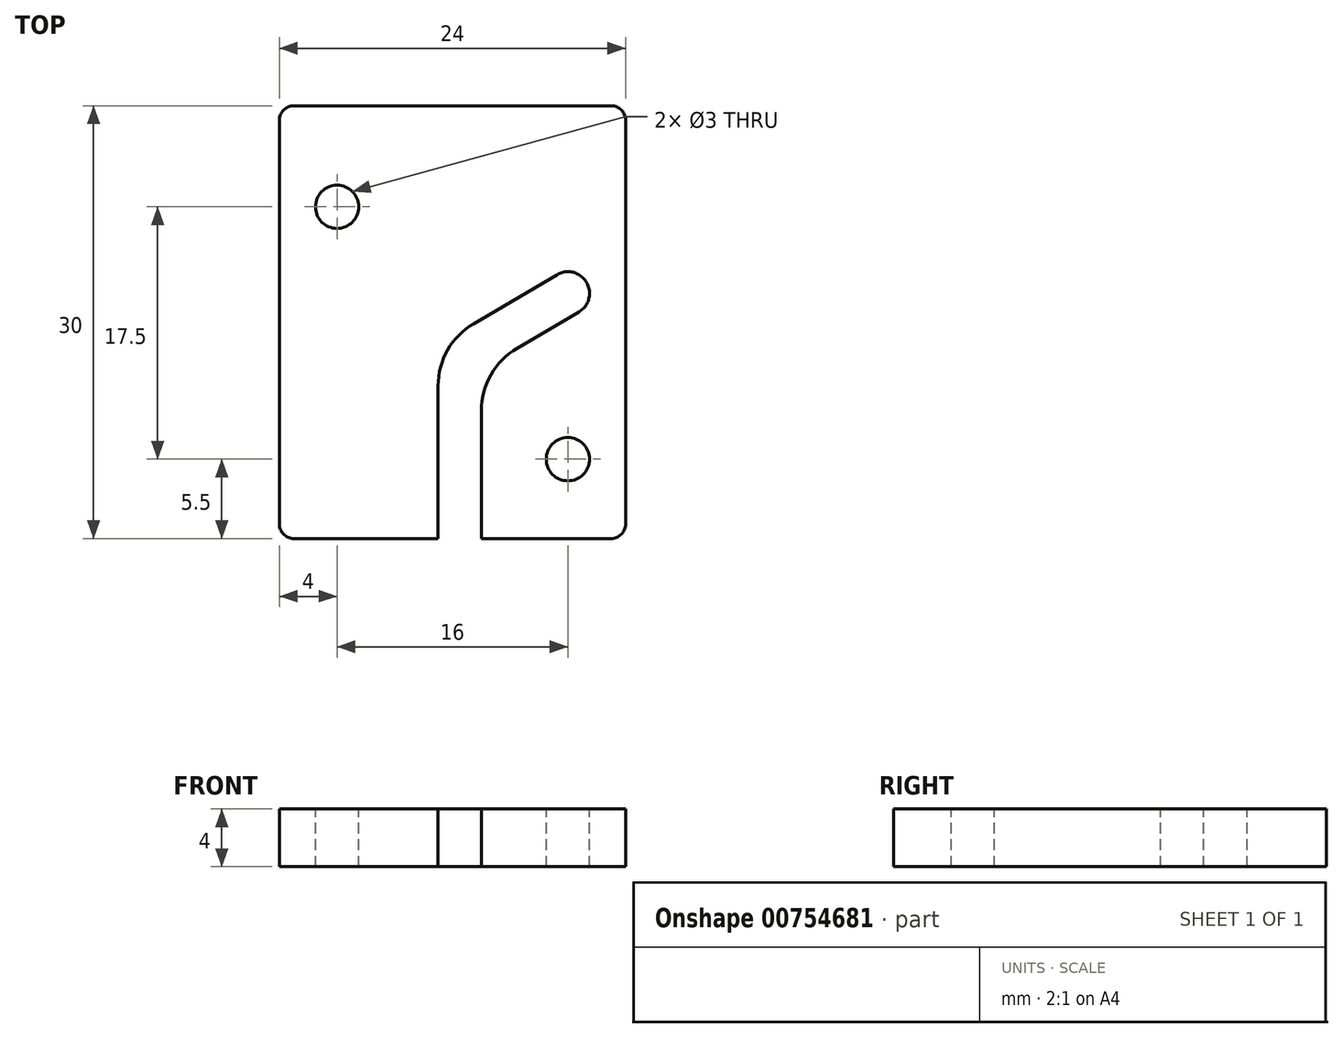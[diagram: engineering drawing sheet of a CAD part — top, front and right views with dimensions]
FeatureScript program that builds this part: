
annotation { "Feature Type Name" : "Feature", "Feature Type Description" : "" }
export const myFeature = defineFeature(function(context is Context, id is Id, definition is map)
    precondition{}
    {
        {
            var Q0;
            Q0=qCreatedBy(makeId("Top.planeOp"),FACE);
            var sketch = newSketch(context, id + "F0", { "sketchPlane" : qUnion([Q0])});
            skLineSegment(sketch, "E0.bottom", {"start": v(1, 0) * mm, "end": v(23, 0) * mm});
            skLineSegment(sketch, "E0.top", {"start": v(1, 30) * mm, "end": v(23, 30) * mm});
            skLineSegment(sketch, "E0.left", {"start": v(0, 1) * mm, "end": v(0, 29) * mm});
            skLineSegment(sketch, "E0.right", {"start": v(24, 1) * mm, "end": v(24, 29) * mm});
            skLineSegment(sketch, "E1", {"start": v(14, 0) * mm, "end": v(14, 8.87) * mm});
            skLineSegment(sketch, "E2", {"start": v(11, 0) * mm, "end": v(11, 10.59) * mm});
            skPoint(sketch, "E3", {"position": v(20, 17) * mm});
            skArc(sketch, "E4", {"start": v(20.76, 15.7) * mm, "mid": v(21.3, 17.76) * mm, "end": v(19.24, 18.3) * mm});
            skLineSegment(sketch, "E5", {"start": v(19.24, 18.3) * mm, "end": v(13.46, 14.9) * mm});
            skLineSegment(sketch, "E6", {"start": v(20.76, 15.7) * mm, "end": v(16.46, 13.18) * mm});
            skArc(sketch, "E7.filletArc", {"start": v(16.46, 13.18) * mm, "mid": v(14.66, 11.35) * mm, "end": v(14, 8.87) * mm});
            skArc(sketch, "E8.filletArc", {"start": v(13.46, 14.9) * mm, "mid": v(11.66, 13.07) * mm, "end": v(11, 10.59) * mm});
            skPoint(sketch, "E9.visualSharp", {"position": v(0, 30) * mm});
            skArc(sketch, "E9.filletArc", {"start": v(1, 30) * mm, "mid": v(0.3, 29.7) * mm, "end": v(0, 29) * mm});
            skPoint(sketch, "E10.visualSharp", {"position": v(0, 0) * mm});
            skArc(sketch, "E10.filletArc", {"start": v(0, 1) * mm, "mid": v(0.3, 0.3) * mm, "end": v(1, 0) * mm});
            skPoint(sketch, "E11.visualSharp", {"position": v(24, 0) * mm});
            skArc(sketch, "E11.filletArc", {"start": v(23, 0) * mm, "mid": v(23.7, 0.3) * mm, "end": v(24, 1) * mm});
            skPoint(sketch, "E12.visualSharp", {"position": v(24, 30) * mm});
            skArc(sketch, "E12.filletArc", {"start": v(24, 29) * mm, "mid": v(23.7, 29.7) * mm, "end": v(23, 30) * mm});
            skPoint(sketch, "E13", {"position": v(4, 23) * mm});
            skPoint(sketch, "E14", {"position": v(20, 5.5) * mm});
            skCircle(sketch, "E15", {"center": v(4, 23) * mm, "radius": 1.5 * mm});
            skCircle(sketch, "E16", {"center": v(20, 5.5) * mm, "radius": 1.5 * mm});
            skSolve(sketch);
        }
        {
            var Q0;
            Q0=makeQuery(id+"F0.imprint","IMPRINT",FACE,{"disambiguationData":[TD([[makeQuery(id+"F0.imprint","IMPRINT",EDGE,{"derivedFrom":sQuery(id+"F0.wireOp",EDGE,"E0.top")}),-1.0]])]});
            extrude(context, id + "F1", {"entities" : qUnion([Q0]), "oppositeDirection" : true, "depth" : 4 * mm, "offsetDistance" : 25 * mm});
        }
    });
